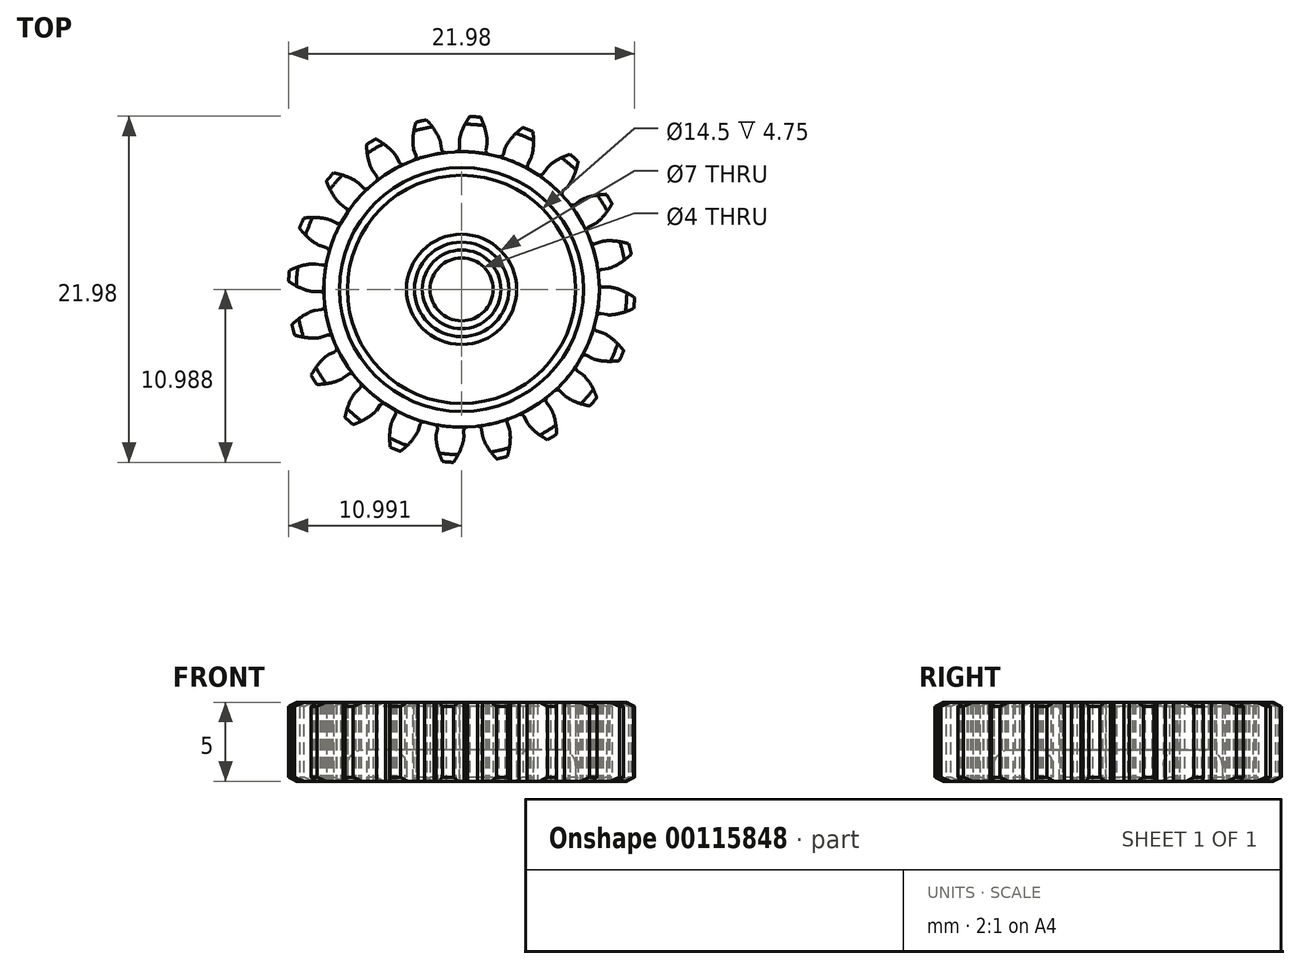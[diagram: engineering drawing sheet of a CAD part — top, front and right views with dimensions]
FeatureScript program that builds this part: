
annotation { "Feature Type Name" : "Feature", "Feature Type Description" : "" }
export const myFeature = defineFeature(function(context is Context, id is Id, definition is map)
    precondition{}
    {
        {
            var Q0;
            Q0=qCreatedBy(makeId("Top.planeOp"),FACE);
            var sketch = newSketch(context, id + "F0", { "sketchPlane" : qUnion([Q0])});
            skArc(sketch, "E0", {"start": v(50.54, -0.96) * mm, "mid": v(50.58, -0.62) * mm, "end": v(50.6, -0.27) * mm});
            skFitSpline(sketch, "E1", {"points": [v(49, 0.39) * mm, v(49, 0.39) * mm, v(49, 0.39) * mm, v(49.01, 0.39) * mm, v(49.02, 0.39) * mm, v(49.03, 0.39) * mm, v(49.04, 0.39) * mm, v(49.06, 0.39) * mm, v(49.08, 0.38) * mm, v(49.1, 0.38) * mm, v(49.12, 0.38) * mm, v(49.15, 0.37) * mm, v(49.18, 0.37) * mm, v(49.21, 0.36) * mm, v(49.25, 0.36) * mm, v(49.29, 0.35) * mm, v(49.33, 0.34) * mm, v(49.37, 0.33) * mm, v(49.41, 0.31) * mm, v(49.46, 0.3) * mm, v(49.51, 0.28) * mm, v(49.57, 0.26) * mm, v(49.62, 0.24) * mm, v(49.68, 0.22) * mm, v(49.74, 0.2) * mm, v(49.8, 0.17) * mm, v(49.86, 0.15) * mm, v(49.93, 0.11) * mm, v(50, 0.08) * mm, v(50.07, 0.05) * mm, v(50.14, 0) * mm, v(50.22, -0.03) * mm, v(50.3, -0.07) * mm, v(50.37, -0.12) * mm, v(50.45, -0.17) * mm, v(50.53, -0.22) * mm, v(50.58, -0.25) * mm, v(50.6, -0.27) * mm]});
            skFitSpline(sketch, "E2", {"points": [v(48.87, -1.36) * mm, v(48.87, -1.36) * mm, v(48.87, -1.36) * mm, v(48.88, -1.36) * mm, v(48.88, -1.36) * mm, v(48.9, -1.36) * mm, v(48.9, -1.36) * mm, v(48.92, -1.37) * mm, v(48.94, -1.37) * mm, v(48.96, -1.37) * mm, v(48.99, -1.37) * mm, v(49.01, -1.37) * mm, v(49.04, -1.37) * mm, v(49.08, -1.37) * mm, v(49.11, -1.37) * mm, v(49.15, -1.36) * mm, v(49.2, -1.36) * mm, v(49.24, -1.36) * mm, v(49.28, -1.35) * mm, v(49.33, -1.34) * mm, v(49.39, -1.33) * mm, v(49.44, -1.33) * mm, v(49.5, -1.31) * mm, v(49.56, -1.3) * mm, v(49.62, -1.29) * mm, v(49.69, -1.27) * mm, v(49.75, -1.25) * mm, v(49.82, -1.23) * mm, v(49.9, -1.21) * mm, v(49.97, -1.19) * mm, v(50.05, -1.16) * mm, v(50.13, -1.13) * mm, v(50.21, -1.1) * mm, v(50.3, -1.07) * mm, v(50.38, -1.03) * mm, v(50.46, -1) * mm, v(50.52, -0.97) * mm, v(50.54, -0.96) * mm]});
            skLineSegment(sketch, "E3", {"start": v(49, 0.39) * mm, "end": v(48.6, 0.38) * mm});
            skLineSegment(sketch, "E4", {"start": v(48.48, -1.3) * mm, "end": v(48.87, -1.36) * mm});
            skArc(sketch, "E5", {"start": v(48.19, -1.49) * mm, "mid": v(30.89, 0.93) * mm, "end": v(48.35, 0.62) * mm});
            skPoint(sketch, "E6.visualSharp", {"position": v(48.36, 0.38) * mm});
            skArc(sketch, "E6.filletArc", {"start": v(48.35, 0.62) * mm, "mid": v(48.43, 0.45) * mm, "end": v(48.6, 0.38) * mm});
            skPoint(sketch, "E7.visualSharp", {"position": v(48.23, -1.25) * mm});
            skArc(sketch, "E7.filletArc", {"start": v(48.48, -1.3) * mm, "mid": v(48.3, -1.33) * mm, "end": v(48.19, -1.49) * mm});
            skCircle(sketch, "E8", {"center": v(39.61, 0.25) * mm, "radius": 8.75 * mm});
            skCircle(sketch, "E9", {"center": v(39.61, 0.25) * mm, "radius": 2 * mm});
            skCircle(sketch, "E10", {"center": v(39.61, 0.25) * mm, "radius": 3.5 * mm});
            skCircle(sketch, "E11", {"center": v(39.61, 0.25) * mm, "radius": 7.25 * mm});
            skText(sketch, "E12", { "text": "PCD=20mm", "fontName": "OpenSans-Regular.ttf"});
            const initialGuessF0  = {"E12": [0.04896, -0.00619, 1, 0, 0.00084]};
            skSetInitialGuess(sketch, initialGuessF0);
            skSolve(sketch);
        }
        {
            var Q0;
            Q0=makeQuery(id+"F0.imprint","IMPRINT",FACE,{"disambiguationData":[TD([[makeQuery(id+"F0.imprint","IMPRINT",EDGE,{"derivedFrom":sQuery(id+"F0.wireOp",EDGE,"E0")}),1.0]])]});
            extrude(context, id + "F1", {"entities" : qUnion([Q0]), "depth" : 5 * mm});
        }
        {
            var Q0;
            Q0=makeQuery(id+"F1.opExtrude","CAP_EDGE",EDGE,{"disambiguationData":[OSD([sQuery(id+"F0.wireOp",EDGE,"E0")])],"isStart":false});
            var Q1;
            Q1=makeQuery(id+"F1.opExtrude","CAP_EDGE",EDGE,{"disambiguationData":[OSD([sQuery(id+"F0.wireOp",EDGE,"E0")])],"isStart":true});
            chamfer(context, id + "F2", {"entities" : qUnion([Q0, Q1]), "chamferType" : ChamferType.TWO_OFFSETS, "width1" : .5 * mm, "oppositeDirection" : false, "width2" : .25 * mm, "tangentPropagation" : true});
        }
        {
            var Q0;
            Q0=makeQuery(id+"F1.opExtrude","SWEPT_BODY",BODY,{"disambiguationData":[OSD([sQuery(id+"F0.wireOp",EDGE,"E0"),sQuery(id+"F0.wireOp",EDGE,"E1"),sQuery(id+"F0.wireOp",EDGE,"E2"),sQuery(id+"F0.wireOp",EDGE,"E3"),sQuery(id+"F0.wireOp",EDGE,"E4"),sQuery(id+"F0.wireOp",EDGE,"E6.filletArc"),sQuery(id+"F0.wireOp",EDGE,"E7.filletArc"),sQuery(id+"F0.wireOp",EDGE,"E8")])]});
            var Q1;
            Q1=sQuery(id+"F0.wireOp",EDGE,"E9");
            circularPattern(context, id + "F3", {"entities" : qUnion([Q0]), "axis" : qUnion([Q1]), "angle" : 18 * degree, "instanceCount" : 20});
        }
        {
            var Q0;
            Q0=makeQuery(id+"F0.imprint","IMPRINT",FACE,{"disambiguationData":[TD([[makeQuery(id+"F0.imprint","IMPRINT",EDGE,{"derivedFrom":sQuery(id+"F0.wireOp",EDGE,"E11")}),-1.0]])]});
            var Q1;
            Q1=makeQuery(id+"F0.imprint","IMPRINT",FACE,{"disambiguationData":[TD([[makeQuery(id+"F0.imprint","IMPRINT",EDGE,{"derivedFrom":sQuery(id+"F0.wireOp",EDGE,"E9")}),-1.0]])]});
            extrude(context, id + "F4", {"entities" : qUnion([Q0, Q1]), "depth" : 5 * mm});
        }
        {
            var Q0;
            Q0=makeQuery(id+"F0.imprint","IMPRINT",FACE,{"disambiguationData":[TD([[makeQuery(id+"F0.imprint","IMPRINT",EDGE,{"derivedFrom":sQuery(id+"F0.wireOp",EDGE,"E10")}),-1.0]])]});
            extrude(context, id + "F5", {"entities" : qUnion([Q0]), "depth" : 2 * mm});
        }
        {
            var Q0;
            Q0=makeQuery(id+"F5.opExtrude","CAP_EDGE",EDGE,{"disambiguationData":[OSD([sQuery(id+"F0.wireOp",EDGE,"E11")])],"isStart":false});
            var Q1;
            Q1=makeQuery(id+"F5.opExtrude","CAP_EDGE",EDGE,{"disambiguationData":[OSD([sQuery(id+"F0.wireOp",EDGE,"E10")])],"isStart":false});
            fillet(context, id + "F6", {"entities" : qUnion([Q0, Q1]), "radius" : 1 * mm, "tangentPropagation" : true, "allowEdgeOverflow" : false});
        }
        {
            var Q0;
            Q0=makeQuery(id+"F4.opExtrude","CAP_EDGE",EDGE,{"disambiguationData":[OSD([sQuery(id+"F0.wireOp",EDGE,"E11")])],"isStart":false});
            var Q1;
            Q1=makeQuery(id+"F4.opExtrude","CAP_EDGE",EDGE,{"disambiguationData":[OSD([sQuery(id+"F0.wireOp",EDGE,"E9")])],"isStart":false});
            chamfer(context, id + "F7", {"entities" : qUnion([Q0, Q1]), "chamferType" : ChamferType.TWO_OFFSETS, "width1" : .25 * mm, "oppositeDirection" : false, "width2" : .5 * mm, "tangentPropagation" : true});
        }
        {
            var Q0;
            Q0=makeQuery(id+"F4.opExtrude","CAP_EDGE",EDGE,{"disambiguationData":[OSD([sQuery(id+"F0.wireOp",EDGE,"E10")])],"isStart":false});
            var Q1;
            Q1=makeQuery(id+"F4.opExtrude","CAP_EDGE",EDGE,{"disambiguationData":[OSD([sQuery(id+"F0.wireOp",EDGE,"E9")])],"isStart":true});
            chamfer(context, id + "F8", {"entities" : qUnion([Q0, Q1]), "chamferType" : ChamferType.TWO_OFFSETS, "width1" : .5 * mm, "oppositeDirection" : false, "width2" : .25 * mm, "tangentPropagation" : true});
        }
    });
